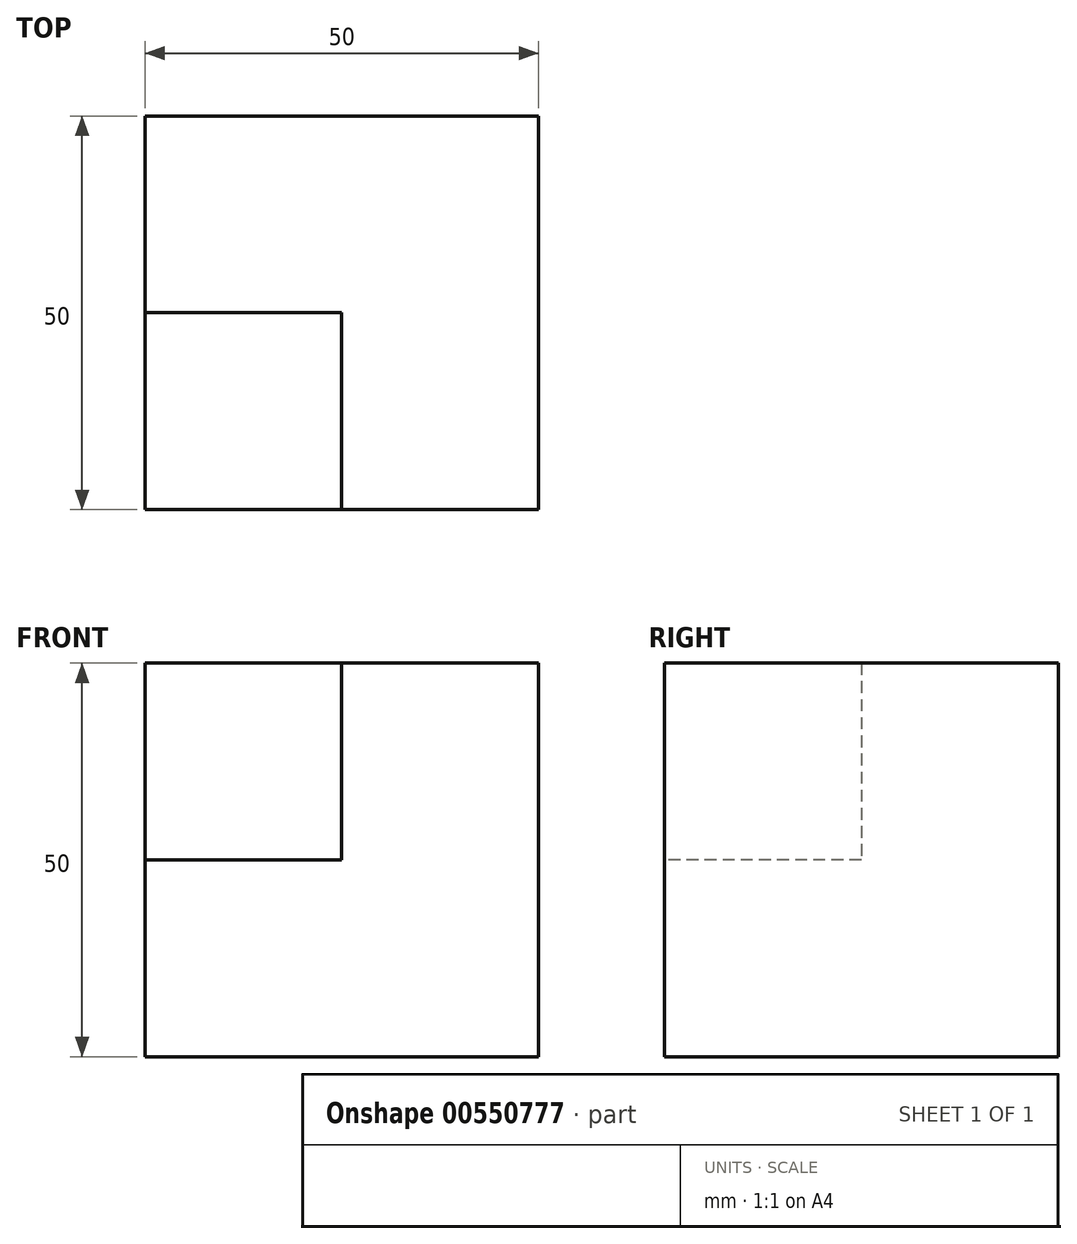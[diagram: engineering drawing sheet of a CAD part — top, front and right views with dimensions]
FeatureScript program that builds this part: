
annotation { "Feature Type Name" : "Feature", "Feature Type Description" : "" }
export const myFeature = defineFeature(function(context is Context, id is Id, definition is map)
    precondition{}
    {
        {
            var Q0;
            Q0=qCreatedBy(makeId("Top.planeOp"),FACE);
            var sketch = newSketch(context, id + "F0", { "sketchPlane" : qUnion([Q0])});
            skLineSegment(sketch, "E0", {"start": v(-44.56, 40.72) * mm, "end": v(-44.56, -9.28) * mm});
            skLineSegment(sketch, "E1", {"start": v(-44.56, -9.28) * mm, "end": v(5.44, -9.28) * mm});
            skLineSegment(sketch, "E2", {"start": v(5.44, -9.28) * mm, "end": v(5.44, 40.72) * mm});
            skLineSegment(sketch, "E3", {"start": v(5.44, 40.72) * mm, "end": v(-44.56, 40.72) * mm});
            skSolve(sketch);
        }
        {
            var Q0;
            Q0 = qSketchRegion(id + "F0", true);
            extrude(context, id + "F1", {"entities" : qUnion([Q0]), "depth" : 50 * mm, "offsetDistance" : 25 * mm});
        }
        {
            var Q0;
            Q0=makeQuery(id+"F1.opExtrude","SWEPT_FACE",FACE,{"disambiguationData":[OSD([sQuery(id+"F0.wireOp",EDGE,"E1")])]});
            var sketch = newSketch(context, id + "F2", { "sketchPlane" : qUnion([Q0])});
            skLineSegment(sketch, "E4.bottom", {"start": v(-44.56, 50) * mm, "end": v(-19.56, 50) * mm});
            skLineSegment(sketch, "E4.top", {"start": v(-44.56, 25) * mm, "end": v(-19.56, 25) * mm});
            skLineSegment(sketch, "E4.left", {"start": v(-44.56, 50) * mm, "end": v(-44.56, 25) * mm});
            skLineSegment(sketch, "E4.right", {"start": v(-19.56, 50) * mm, "end": v(-19.56, 25) * mm});
            skSolve(sketch);
        }
        {
            var Q0;
            Q0 = qSketchRegion(id + "F2", true);
            extrude(context, id + "F3", {"entities" : qUnion([Q0]), "operationType" : NewBodyOperationType.REMOVE, "oppositeDirection" : true, "depth" : 25 * mm, "offsetDistance" : 25 * mm});
        }
    });
